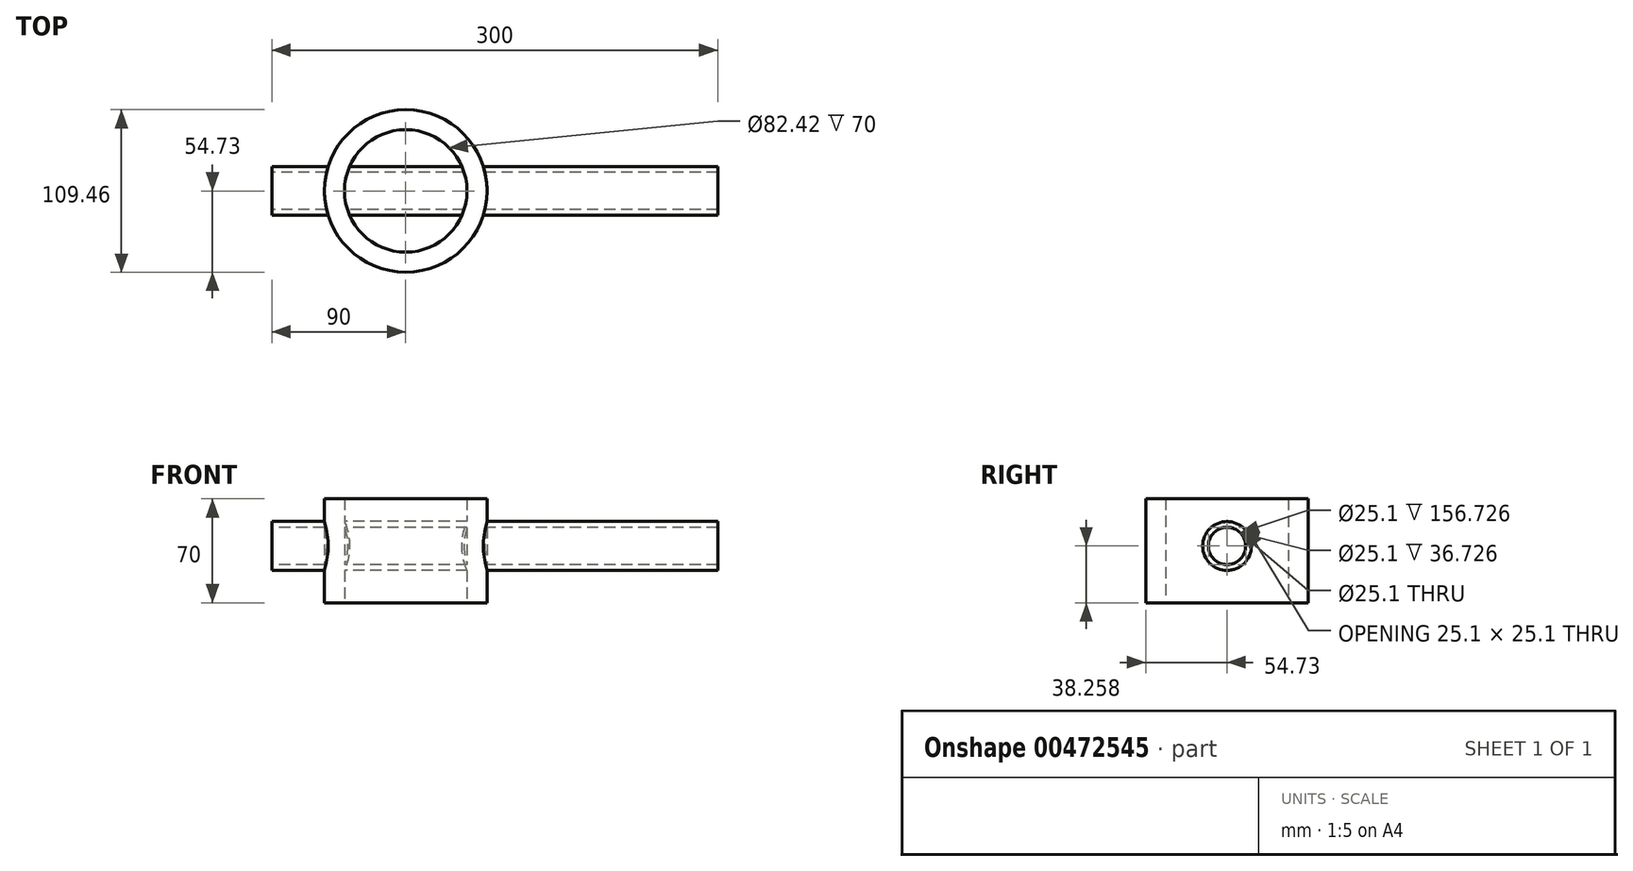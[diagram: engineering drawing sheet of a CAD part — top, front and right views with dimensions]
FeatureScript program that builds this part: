
annotation { "Feature Type Name" : "Feature", "Feature Type Description" : "" }
export const myFeature = defineFeature(function(context is Context, id is Id, definition is map)
    precondition{}
    {
        {
            var Q0;
            Q0=qCreatedBy(makeId("Top.planeOp"),FACE);
            var sketch = newSketch(context, id + "F0", { "sketchPlane" : qUnion([Q0])});
            skCircle(sketch, "E0", {"center": v(0, 0) * mm, "radius": 54.73 * mm});
            skCircle(sketch, "E1", {"center": v(0, 0) * mm, "radius": 41.2 * mm});
            skSolve(sketch);
        }
        {
            var Q0;
            Q0=makeQuery(id+"F0.imprint","IMPRINT",FACE,{"disambiguationData":[TD([[makeQuery(id+"F0.imprint","IMPRINT",EDGE,{"derivedFrom":sQuery(id+"F0.wireOp",EDGE,"E0")}),1.0]])]});
            extrude(context, id + "F1", {"entities" : qUnion([Q0]), "depth" : 70 * mm});
        }
        {
            var Q0;
            Q0=qCreatedBy(makeId("Right.planeOp"),FACE);
            var sketch = newSketch(context, id + "F2", { "sketchPlane" : qUnion([Q0])});
            skCircle(sketch, "E2", {"center": v(0, 38.26) * mm, "radius": 16.43 * mm});
            skCircle(sketch, "E3", {"center": v(0, 38.26) * mm, "radius": 12.55 * mm});
            skSolve(sketch);
        }
        {
            var Q0;
            Q0 = qSketchRegion(id + "F2", true);
            extrude(context, id + "F3", {"entities" : qUnion([Q0]), "operationType" : NewBodyOperationType.ADD, "depth" : 60 * mm});
        }
        {
            var Q0;
            Q0=makeQuery(id+"F3.opExtrude","CAP_FACE",FACE,{"disambiguationData":[OSD([sQuery(id+"F2.wireOp",EDGE,"E2"),sQuery(id+"F2.wireOp",EDGE,"E3")])],"isStart":false});
            extrude(context, id + "F4", {"entities" : qUnion([Q0]), "operationType" : NewBodyOperationType.ADD, "endBound" : BoundingType.SYMMETRIC, "depth" : 300 * mm});
        }
    });
